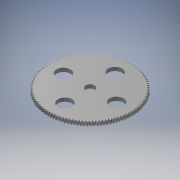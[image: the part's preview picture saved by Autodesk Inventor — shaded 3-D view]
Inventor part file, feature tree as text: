
AUTODESK INVENTOR PART (.ipt)
format: ipt  version: 2018.3 (Build 223284000, 284)  size: 618,496 bytes
history: native  units: mm (DEFAULTED — no unit token found)
features: other x7, plane x3, sketch x2, reference x2, extrude x1
ambient origin geometry x8: Origin, YZ Plane, XZ Plane, XY Plane, X Axis, Y Axis, Z Axis, Center Point
bodies: Solid1 (feature_tree)
feature tree (15):
  extrude  "Extrusion1"  Depth=10.0mm TaperAngle=0.0deg
  plane  "Work Plane2"
  plane  "Work Plane8"
  plane  "Work Plane9"
  other  "Цилиндрическое зубчатое зацепление"
  sketch  "Sketch1"  dims[d0=227.833495mm d1=10.0mm d2=0.0mm]
  sketch  "Sketch2"  dims[d3=222.635528mm d4=10.0mm d5=0.0mm d16=161.916747mm d17=0.0mm d34=0.285599mm d39=0.0mm d41=0.0mm d43=161.916747mm d46=161.916747mm d47=0.0mm d48=0.0mm d49=40.0mm d51=360.0deg]
  other  "Srf1"
  reference  "Ссылка1"
  reference  "Ссылка2"
  other  "Средний диаметр"
  other  "<userpath>\My_projects\Al.Mechanic.CoffeeMachine\Сборка.iam"
  other  "Сборка.iam"
  other  "Фильтр:1"
  other  "Ось:1"
